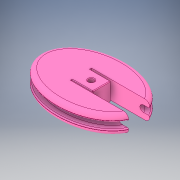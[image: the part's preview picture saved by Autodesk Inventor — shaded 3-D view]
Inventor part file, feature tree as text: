
AUTODESK INVENTOR PART (.ipt)
format: ipt  version: 2017 SP1 (Build 210196100, 196)  size: 395,264 bytes
history: native  units: in
note: dims shown in document units (in); Inventor stores cm internally (conversion verified against a paired STEP export)
features: sketch x4, extrude x2, sweep x1, chamfer x1
ambient origin geometry x8: Origin, YZ Plane, XZ Plane, XY Plane, X Axis, Y Axis, Z Axis, Center Point
bodies: Solid1 (feature_tree)
feature tree (8):
  sweep  "Sweep1"
  extrude  "Extrusion1"  Depth=0.05in
  extrude  "Extrusion2"  Depth=2.0in
  chamfer  "Chamfer1"  [1 undecoded]
  sketch  "Sketch1"  dims[d1=0.875in d5=0.25in]
  sketch  "Sketch2"  dims[d6=0.3125in d7=0.05in]
  sketch  "Sketch3"  dims[d8=0.22in d9=2.0in]
  sketch  "Sketch4"  dims[d10=1.25in d11=0.0in d12=0.0in d13=0.875in d14=0.0in d19=0.875in d20=0.0in d23=0.26in d25=0.5in d26=0.5in d27=0.87in d29=4.0in d30=0.5in d31=2.0in d32=1.015in d33=0.03in d34=0.125in d35=45.0deg]
note: 1 required parameter value undecoded (feature->parameter linkage not recoverable at this tier; creation-order binding heuristic only, values carry confidence <= 0.55)
